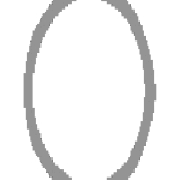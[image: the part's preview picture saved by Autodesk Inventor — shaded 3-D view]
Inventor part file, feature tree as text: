
AUTODESK INVENTOR PART (.ipt)
format: ipt  version: 2021 (Build 250183000, 183)  size: 112,640 bytes
history: native  units: in
note: dims shown in document units (in); Inventor stores cm internally (conversion verified against a paired STEP export)
features: other x4, sketch x3, plane x1
ambient origin geometry x8: Origin, YZ Plane, XZ Plane, XY Plane, X Axis, Y Axis, Z Axis, Center Point
bodies: Solid1 (feature_tree), Body (feature_tree)
feature tree (8):
  other  "Driven Length"
  other  "Frame Generator"
  other  "Start Plane"
  other  "End Plane"
  sketch  "Sketch"  dims[d2=11.6851in d4=-0.0in d5=11.6851in d6=0.12in d7=0.0in d8=90.0deg d9=11.6851in]
  sketch  "Sketch2"  dims[d0=1.0in]
  plane  "Work Plane3"
  sketch  "Sketch3"  dims[d1=0.065in]
